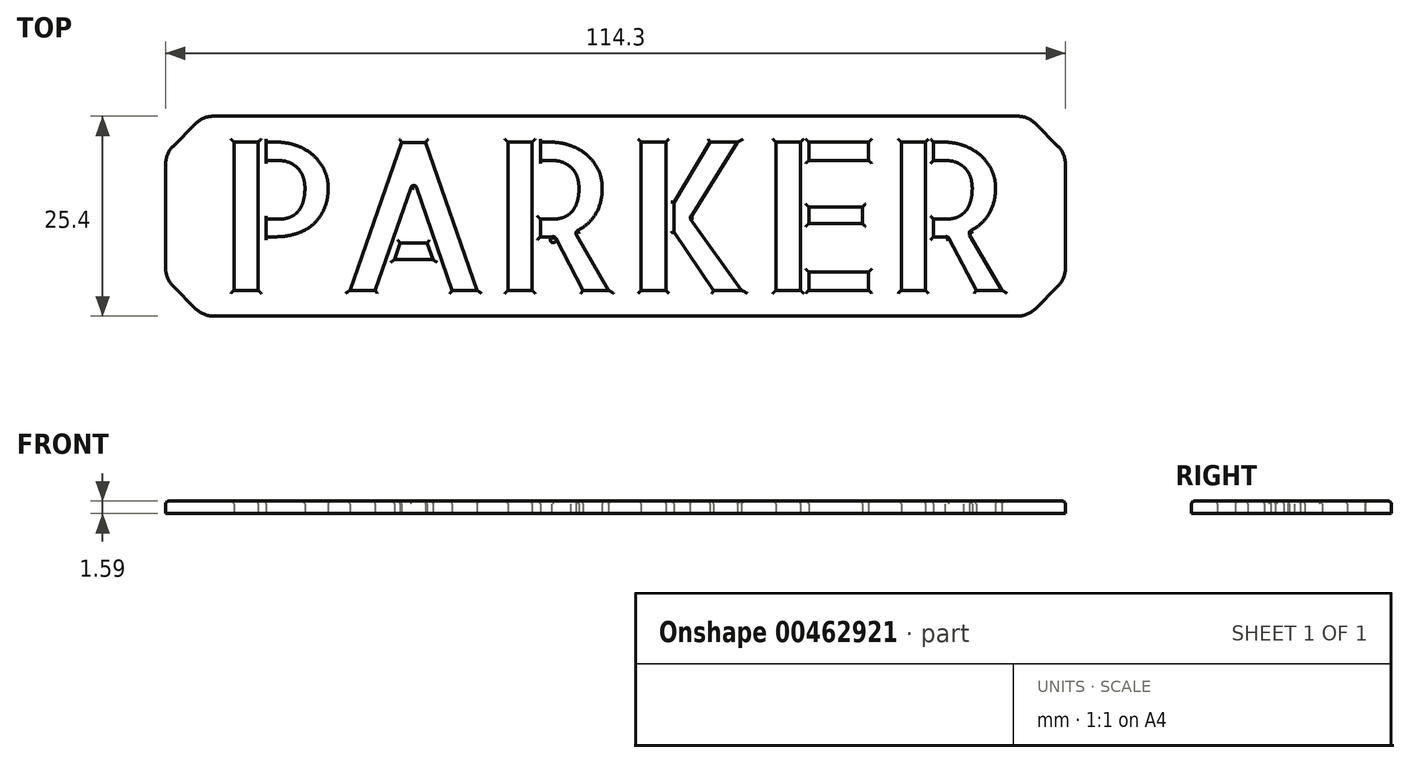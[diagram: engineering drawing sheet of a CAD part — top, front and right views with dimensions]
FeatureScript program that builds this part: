
annotation { "Feature Type Name" : "Feature", "Feature Type Description" : "" }
export const myFeature = defineFeature(function(context is Context, id is Id, definition is map)
    precondition{}
    {
        {
            var Q0;
            Q0=qCreatedBy(makeId("Top.planeOp"),FACE);
            var sketch = newSketch(context, id + "F0", { "sketchPlane" : qUnion([Q0])});
            skText(sketch, "E0", { "text": "PARKER", "fontName": "AllertaStencil-Regular.ttf"});
            skLineSegment(sketch, "E1.bottom", {"start": v(-6.35, 22.11) * mm, "end": v(107.95, 22.11) * mm});
            skLineSegment(sketch, "E1.top", {"start": v(-6.35, -3.29) * mm, "end": v(107.95, -3.29) * mm});
            skLineSegment(sketch, "E1.left", {"start": v(-6.35, 22.11) * mm, "end": v(-6.35, -3.29) * mm});
            skLineSegment(sketch, "E1.right", {"start": v(107.95, 22.11) * mm, "end": v(107.95, -3.29) * mm});
            skLineSegment(sketch, "E2", {"start": v(50.8, 18.83) * mm, "end": v(50.8, 22.11) * mm, "construction": true});
            skLineSegment(sketch, "E3", {"start": v(50.8, -3.29) * mm, "end": v(50.8, 0) * mm, "construction": true});
            const initialGuessF0  = {"E0": [0, 0, 1, 0, 0.01883]};
            skSetInitialGuess(sketch, initialGuessF0);
            skSolve(sketch);
        }
        {
            var Q0;
            Q0=qSketchRegion(id+"F0",true);
            extrude(context, id + "F1", {"entities" : qUnion([Q0]), "depth" : 1.59 * mm});
        }
        {
            var Q0;
            Q0=makeQuery(id+"F1.opExtrude","SWEPT_EDGE",EDGE,{"disambiguationData":[OSD([sQuery(id+"F0.wireOp",EDGE,"E1.bottom"),sQuery(id+"F0.wireOp",EDGE,"E1.right")])]});
            var Q1;
            Q1=makeQuery(id+"F1.opExtrude","SWEPT_EDGE",EDGE,{"disambiguationData":[OSD([sQuery(id+"F0.wireOp",EDGE,"E1.top"),sQuery(id+"F0.wireOp",EDGE,"E1.right")])]});
            var Q2;
            Q2=makeQuery(id+"F1.opExtrude","SWEPT_EDGE",EDGE,{"disambiguationData":[OSD([sQuery(id+"F0.wireOp",EDGE,"E1.top"),sQuery(id+"F0.wireOp",EDGE,"E1.left")])]});
            var Q3;
            Q3=makeQuery(id+"F1.opExtrude","SWEPT_EDGE",EDGE,{"disambiguationData":[OSD([sQuery(id+"F0.wireOp",EDGE,"E1.bottom"),sQuery(id+"F0.wireOp",EDGE,"E1.left")])]});
            chamfer(context, id + "F2", {"entities" : qUnion([Q0, Q1, Q2, Q3]), "width" : 4.76 * mm, "tangentPropagation" : true});
        }
        {
            var Q0;
            Q0=makeQuery(id+"F1.opExtrude","CAP_EDGE",EDGE,{"disambiguationData":[OSD([sQuery(id+"F0.wireOp",EDGE,"E0.sketch_text.stroke-17")])],"isStart":false});
            var Q1;
            Q1=makeQuery(id+"F1.opExtrude","CAP_EDGE",EDGE,{"disambiguationData":[OSD([sQuery(id+"F0.wireOp",EDGE,"E0.sketch_text.stroke-11")])],"isStart":false});
            var Q2;
            Q2=makeQuery(id+"F1.opExtrude","CAP_EDGE",EDGE,{"disambiguationData":[OSD([sQuery(id+"F0.wireOp",EDGE,"E0.sketch_text.stroke-10")])],"isStart":false});
            var Q3;
            Q3=makeQuery(id+"F1.opExtrude","CAP_EDGE",EDGE,{"disambiguationData":[OSD([sQuery(id+"F0.wireOp",EDGE,"E0.sketch_text.stroke-37")])],"isStart":false});
            var Q4;
            Q4=makeQuery(id+"F1.opExtrude","CAP_EDGE",EDGE,{"disambiguationData":[OSD([sQuery(id+"F0.wireOp",EDGE,"E0.sketch_text.stroke-29")])],"isStart":false});
            var Q5;
            Q5=makeQuery(id+"F1.opExtrude","CAP_EDGE",EDGE,{"disambiguationData":[OSD([sQuery(id+"F0.wireOp",EDGE,"E0.sketch_text.stroke-28")])],"isStart":false});
            var Q6;
            Q6=makeQuery(id+"F1.opExtrude","CAP_EDGE",EDGE,{"disambiguationData":[OSD([sQuery(id+"F0.wireOp",EDGE,"E0.sketch_text.stroke-18")])],"isStart":false});
            var Q7;
            Q7=makeQuery(id+"F1.opExtrude","CAP_EDGE",EDGE,{"disambiguationData":[OSD([sQuery(id+"F0.wireOp",EDGE,"E0.sketch_text.stroke-0")])],"isStart":false});
            var Q8;
            Q8=makeQuery(id+"F1.opExtrude","CAP_EDGE",EDGE,{"disambiguationData":[OSD([sQuery(id+"F0.wireOp",EDGE,"E0.sketch_text.stroke-3")])],"isStart":false});
            var Q9;
            Q9=makeQuery(id+"F1.opExtrude","CAP_EDGE",EDGE,{"disambiguationData":[OSD([sQuery(id+"F0.wireOp",EDGE,"E0.sketch_text.stroke-1")])],"isStart":false});
            var Q10;
            Q10=makeQuery(id+"F1.opExtrude","CAP_EDGE",EDGE,{"disambiguationData":[OSD([sQuery(id+"F0.wireOp",EDGE,"E0.sketch_text.stroke-2")])],"isStart":false});
            fillet(context, id + "F3", {"entities" : qUnion([Q0, Q1, Q2, Q3, Q4, Q5, Q6, Q7, Q8, Q9, Q10]), "radius" : 0.38 * mm, "tangentPropagation" : true, "allowEdgeOverflow" : false});
        }
        {
            var Q0;
            Q0=makeQuery(id+"F1.opExtrude","CAP_EDGE",EDGE,{"disambiguationData":[OSD([sQuery(id+"F0.wireOp",EDGE,"E0.sketch_text.stroke-53")])],"isStart":false});
            var Q1;
            Q1=makeQuery(id+"F1.opExtrude","CAP_EDGE",EDGE,{"disambiguationData":[OSD([sQuery(id+"F0.wireOp",EDGE,"E0.sketch_text.stroke-54")])],"isStart":false});
            var Q2;
            Q2=makeQuery(id+"F1.opExtrude","CAP_EDGE",EDGE,{"disambiguationData":[OSD([sQuery(id+"F0.wireOp",EDGE,"E0.sketch_text.stroke-64")])],"isStart":false});
            var Q3;
            Q3=makeQuery(id+"F1.opExtrude","CAP_EDGE",EDGE,{"disambiguationData":[OSD([sQuery(id+"F0.wireOp",EDGE,"E0.sketch_text.stroke-65")])],"isStart":false});
            var Q4;
            Q4=makeQuery(id+"F1.opExtrude","CAP_EDGE",EDGE,{"disambiguationData":[OSD([sQuery(id+"F0.wireOp",EDGE,"E0.sketch_text.stroke-72")])],"isStart":false});
            var Q5;
            Q5=makeQuery(id+"F1.opExtrude","CAP_EDGE",EDGE,{"disambiguationData":[OSD([sQuery(id+"F0.wireOp",EDGE,"E0.sketch_text.stroke-47")])],"isStart":false});
            var Q6;
            Q6=makeQuery(id+"F1.opExtrude","CAP_EDGE",EDGE,{"disambiguationData":[OSD([sQuery(id+"F0.wireOp",EDGE,"E0.sketch_text.stroke-48")])],"isStart":false});
            var Q7;
            Q7=makeQuery(id+"F1.opExtrude","CAP_EDGE",EDGE,{"disambiguationData":[OSD([sQuery(id+"F0.wireOp",EDGE,"E0.sketch_text.stroke-31")])],"isStart":false});
            var Q8;
            Q8=makeQuery(id+"F1.opExtrude","CAP_EDGE",EDGE,{"disambiguationData":[OSD([sQuery(id+"F0.wireOp",EDGE,"E0.sketch_text.stroke-30")])],"isStart":false});
            var Q9;
            Q9=makeQuery(id+"F1.opExtrude","CAP_EDGE",EDGE,{"disambiguationData":[OSD([sQuery(id+"F0.wireOp",EDGE,"E0.sketch_text.stroke-32")])],"isStart":false});
            var Q10;
            Q10=makeQuery(id+"F1.opExtrude","CAP_EDGE",EDGE,{"disambiguationData":[OSD([sQuery(id+"F0.wireOp",EDGE,"E0.sketch_text.stroke-26")])],"isStart":false});
            var Q11;
            Q11=makeQuery(id+"F1.opExtrude","CAP_EDGE",EDGE,{"disambiguationData":[OSD([sQuery(id+"F0.wireOp",EDGE,"E0.sketch_text.stroke-27")])],"isStart":false});
            var Q12;
            Q12=makeQuery(id+"F1.opExtrude","CAP_EDGE",EDGE,{"disambiguationData":[OSD([sQuery(id+"F0.wireOp",EDGE,"E0.sketch_text.stroke-36")])],"isStart":false});
            var Q13;
            Q13=makeQuery(id+"F1.opExtrude","CAP_EDGE",EDGE,{"disambiguationData":[OSD([sQuery(id+"F0.wireOp",EDGE,"E0.sketch_text.stroke-35")])],"isStart":false});
            var Q14;
            Q14=makeQuery(id+"F1.opExtrude","CAP_EDGE",EDGE,{"disambiguationData":[OSD([sQuery(id+"F0.wireOp",EDGE,"E0.sketch_text.stroke-34")])],"isStart":false});
            var Q15;
            Q15=makeQuery(id+"F1.opExtrude","CAP_EDGE",EDGE,{"disambiguationData":[OSD([sQuery(id+"F0.wireOp",EDGE,"E0.sketch_text.stroke-33")])],"isStart":false});
            fillet(context, id + "F4", {"entities" : qUnion([Q0, Q1, Q2, Q3, Q4, Q5, Q6, Q7, Q8, Q9, Q10, Q11, Q12, Q13, Q14, Q15]), "radius" : 0.38 * mm, "tangentPropagation" : true, "allowEdgeOverflow" : false});
        }
        {
            var Q0;
            Q0=makeQuery(id+"F1.opExtrude","CAP_EDGE",EDGE,{"disambiguationData":[OSD([sQuery(id+"F0.wireOp",EDGE,"E0.sketch_text.stroke-112")])],"isStart":false});
            var Q1;
            Q1=makeQuery(id+"F1.opExtrude","CAP_EDGE",EDGE,{"disambiguationData":[OSD([sQuery(id+"F0.wireOp",EDGE,"E0.sketch_text.stroke-122")])],"isStart":false});
            var Q2;
            Q2=makeQuery(id+"F1.opExtrude","CAP_EDGE",EDGE,{"disambiguationData":[OSD([sQuery(id+"F0.wireOp",EDGE,"E0.sketch_text.stroke-121")])],"isStart":false});
            var Q3;
            Q3=makeQuery(id+"F1.opExtrude","CAP_EDGE",EDGE,{"disambiguationData":[OSD([sQuery(id+"F0.wireOp",EDGE,"E0.sketch_text.stroke-117")])],"isStart":false});
            var Q4;
            Q4=makeQuery(id+"F1.opExtrude","CAP_EDGE",EDGE,{"disambiguationData":[OSD([sQuery(id+"F0.wireOp",EDGE,"E0.sketch_text.stroke-113")])],"isStart":false});
            var Q5;
            Q5=makeQuery(id+"F1.opExtrude","CAP_EDGE",EDGE,{"disambiguationData":[OSD([sQuery(id+"F0.wireOp",EDGE,"E0.sketch_text.stroke-144")])],"isStart":false});
            var Q6;
            Q6=makeQuery(id+"F1.opExtrude","CAP_EDGE",EDGE,{"disambiguationData":[OSD([sQuery(id+"F0.wireOp",EDGE,"E0.sketch_text.stroke-143")])],"isStart":false});
            var Q7;
            Q7=makeQuery(id+"F1.opExtrude","CAP_EDGE",EDGE,{"disambiguationData":[OSD([sQuery(id+"F0.wireOp",EDGE,"E0.sketch_text.stroke-139")])],"isStart":false});
            var Q8;
            Q8=makeQuery(id+"F1.opExtrude","CAP_EDGE",EDGE,{"disambiguationData":[OSD([sQuery(id+"F0.wireOp",EDGE,"E0.sketch_text.stroke-135")])],"isStart":false});
            var Q9;
            Q9=makeQuery(id+"F1.opExtrude","CAP_EDGE",EDGE,{"disambiguationData":[OSD([sQuery(id+"F0.wireOp",EDGE,"E0.sketch_text.stroke-134")])],"isStart":false});
            fillet(context, id + "F5", {"entities" : qUnion([Q0, Q1, Q2, Q3, Q4, Q5, Q6, Q7, Q8, Q9]), "radius" : 0.38 * mm, "tangentPropagation" : true, "allowEdgeOverflow" : false});
        }
        {
            var Q0;
            {var subQ0=sQuery(id+"F0.wireOp",EDGE,"E1.bottom");Q0=makeQuery(id+"F2.opChamfer","BLEND_EDGE",EDGE,{"blendedFrom":[makeQuery(id+"F1.opExtrude","SWEPT_EDGE",EDGE,{"disambiguationData":[OSD([subQ0,sQuery(id+"F0.wireOp",EDGE,"E1.right")])]}),makeQuery(id+"F1.opExtrude","SWEPT_FACE",FACE,{"disambiguationData":[OSD([subQ0])]})],"blendedInto":[makeQuery(id+"F1.opExtrude","SWEPT_FACE",FACE,{"disambiguationData":[OSD([subQ0])]})]});}
            var Q1;
            {var subQ0=sQuery(id+"F0.wireOp",EDGE,"E1.right");Q1=makeQuery(id+"F2.opChamfer","BLEND_EDGE",EDGE,{"blendedFrom":[makeQuery(id+"F1.opExtrude","SWEPT_EDGE",EDGE,{"disambiguationData":[OSD([sQuery(id+"F0.wireOp",EDGE,"E1.bottom"),subQ0])]}),makeQuery(id+"F1.opExtrude","SWEPT_FACE",FACE,{"disambiguationData":[OSD([subQ0])]})],"blendedInto":[makeQuery(id+"F1.opExtrude","SWEPT_FACE",FACE,{"disambiguationData":[OSD([subQ0])]})]});}
            var Q2;
            {var subQ0=sQuery(id+"F0.wireOp",EDGE,"E1.right");Q2=makeQuery(id+"F2.opChamfer","BLEND_EDGE",EDGE,{"blendedFrom":[makeQuery(id+"F1.opExtrude","SWEPT_EDGE",EDGE,{"disambiguationData":[OSD([sQuery(id+"F0.wireOp",EDGE,"E1.top"),subQ0])]}),makeQuery(id+"F1.opExtrude","SWEPT_FACE",FACE,{"disambiguationData":[OSD([subQ0])]})],"blendedInto":[makeQuery(id+"F1.opExtrude","SWEPT_FACE",FACE,{"disambiguationData":[OSD([subQ0])]})]});}
            var Q3;
            {var subQ0=sQuery(id+"F0.wireOp",EDGE,"E1.top");Q3=makeQuery(id+"F2.opChamfer","BLEND_EDGE",EDGE,{"blendedFrom":[makeQuery(id+"F1.opExtrude","SWEPT_EDGE",EDGE,{"disambiguationData":[OSD([subQ0,sQuery(id+"F0.wireOp",EDGE,"E1.right")])]}),makeQuery(id+"F1.opExtrude","SWEPT_FACE",FACE,{"disambiguationData":[OSD([subQ0])]})],"blendedInto":[makeQuery(id+"F1.opExtrude","SWEPT_FACE",FACE,{"disambiguationData":[OSD([subQ0])]})]});}
            var Q4;
            {var subQ0=sQuery(id+"F0.wireOp",EDGE,"E1.top");Q4=makeQuery(id+"F2.opChamfer","BLEND_EDGE",EDGE,{"blendedFrom":[makeQuery(id+"F1.opExtrude","SWEPT_EDGE",EDGE,{"disambiguationData":[OSD([subQ0,sQuery(id+"F0.wireOp",EDGE,"E1.left")])]}),makeQuery(id+"F1.opExtrude","SWEPT_FACE",FACE,{"disambiguationData":[OSD([subQ0])]})],"blendedInto":[makeQuery(id+"F1.opExtrude","SWEPT_FACE",FACE,{"disambiguationData":[OSD([subQ0])]})]});}
            var Q5;
            {var subQ0=sQuery(id+"F0.wireOp",EDGE,"E1.left");Q5=makeQuery(id+"F2.opChamfer","BLEND_EDGE",EDGE,{"blendedFrom":[makeQuery(id+"F1.opExtrude","SWEPT_EDGE",EDGE,{"disambiguationData":[OSD([sQuery(id+"F0.wireOp",EDGE,"E1.top"),subQ0])]}),makeQuery(id+"F1.opExtrude","SWEPT_FACE",FACE,{"disambiguationData":[OSD([subQ0])]})],"blendedInto":[makeQuery(id+"F1.opExtrude","SWEPT_FACE",FACE,{"disambiguationData":[OSD([subQ0])]})]});}
            var Q6;
            {var subQ0=sQuery(id+"F0.wireOp",EDGE,"E1.left");Q6=makeQuery(id+"F2.opChamfer","BLEND_EDGE",EDGE,{"blendedFrom":[makeQuery(id+"F1.opExtrude","SWEPT_EDGE",EDGE,{"disambiguationData":[OSD([sQuery(id+"F0.wireOp",EDGE,"E1.bottom"),subQ0])]}),makeQuery(id+"F1.opExtrude","SWEPT_FACE",FACE,{"disambiguationData":[OSD([subQ0])]})],"blendedInto":[makeQuery(id+"F1.opExtrude","SWEPT_FACE",FACE,{"disambiguationData":[OSD([subQ0])]})]});}
            var Q7;
            {var subQ0=sQuery(id+"F0.wireOp",EDGE,"E1.bottom");Q7=makeQuery(id+"F2.opChamfer","BLEND_EDGE",EDGE,{"blendedFrom":[makeQuery(id+"F1.opExtrude","SWEPT_EDGE",EDGE,{"disambiguationData":[OSD([subQ0,sQuery(id+"F0.wireOp",EDGE,"E1.left")])]}),makeQuery(id+"F1.opExtrude","SWEPT_FACE",FACE,{"disambiguationData":[OSD([subQ0])]})],"blendedInto":[makeQuery(id+"F1.opExtrude","SWEPT_FACE",FACE,{"disambiguationData":[OSD([subQ0])]})]});}
            fillet(context, id + "F6", {"entities" : qUnion([Q0, Q1, Q2, Q3, Q4, Q5, Q6, Q7]), "radius" : 3.17 * mm, "tangentPropagation" : true, "allowEdgeOverflow" : false});
        }
        {
            var Q0;
            Q0=makeQuery(id+"F1.opExtrude","CAP_EDGE",EDGE,{"disambiguationData":[OSD([sQuery(id+"F0.wireOp",EDGE,"E1.bottom")])],"isStart":false});
            fillet(context, id + "F7", {"entities" : qUnion([Q0]), "radius" : 0.38 * mm, "tangentPropagation" : true, "allowEdgeOverflow" : false});
        }
        {
            var Q0;
            Q0=makeQuery(id+"F1.opExtrude","CAP_EDGE",EDGE,{"disambiguationData":[OSD([sQuery(id+"F0.wireOp",EDGE,"E0.sketch_text.stroke-40")])],"isStart":false});
            var Q1;
            Q1=makeQuery(id+"F1.opExtrude","CAP_EDGE",EDGE,{"disambiguationData":[OSD([sQuery(id+"F0.wireOp",EDGE,"E0.sketch_text.stroke-38")])],"isStart":false});
            var Q2;
            Q2=makeQuery(id+"F1.opExtrude","CAP_EDGE",EDGE,{"disambiguationData":[OSD([sQuery(id+"F0.wireOp",EDGE,"E0.sketch_text.stroke-39")])],"isStart":false});
            var Q3;
            Q3=makeQuery(id+"F1.opExtrude","CAP_EDGE",EDGE,{"disambiguationData":[OSD([sQuery(id+"F0.wireOp",EDGE,"E0.sketch_text.stroke-67")])],"isStart":false});
            var Q4;
            Q4=makeQuery(id+"F1.opExtrude","CAP_EDGE",EDGE,{"disambiguationData":[OSD([sQuery(id+"F0.wireOp",EDGE,"E0.sketch_text.stroke-68")])],"isStart":false});
            var Q5;
            Q5=makeQuery(id+"F1.opExtrude","CAP_EDGE",EDGE,{"disambiguationData":[OSD([sQuery(id+"F0.wireOp",EDGE,"E0.sketch_text.stroke-69")])],"isStart":false});
            var Q6;
            Q6=makeQuery(id+"F1.opExtrude","CAP_EDGE",EDGE,{"disambiguationData":[OSD([sQuery(id+"F0.wireOp",EDGE,"E0.sketch_text.stroke-70")])],"isStart":false});
            var Q7;
            Q7=makeQuery(id+"F1.opExtrude","CAP_EDGE",EDGE,{"disambiguationData":[OSD([sQuery(id+"F0.wireOp",EDGE,"E0.sketch_text.stroke-75")])],"isStart":false});
            var Q8;
            Q8=makeQuery(id+"F1.opExtrude","CAP_EDGE",EDGE,{"disambiguationData":[OSD([sQuery(id+"F0.wireOp",EDGE,"E0.sketch_text.stroke-76")])],"isStart":false});
            var Q9;
            Q9=makeQuery(id+"F1.opExtrude","CAP_EDGE",EDGE,{"disambiguationData":[OSD([sQuery(id+"F0.wireOp",EDGE,"E0.sketch_text.stroke-77")])],"isStart":false});
            var Q10;
            Q10=makeQuery(id+"F1.opExtrude","CAP_EDGE",EDGE,{"disambiguationData":[OSD([sQuery(id+"F0.wireOp",EDGE,"E0.sketch_text.stroke-71")])],"isStart":false});
            var Q11;
            Q11=makeQuery(id+"F1.opExtrude","CAP_EDGE",EDGE,{"disambiguationData":[OSD([sQuery(id+"F0.wireOp",EDGE,"E0.sketch_text.stroke-73")])],"isStart":false});
            var Q12;
            Q12=makeQuery(id+"F1.opExtrude","CAP_EDGE",EDGE,{"disambiguationData":[OSD([sQuery(id+"F0.wireOp",EDGE,"E0.sketch_text.stroke-74")])],"isStart":false});
            var Q13;
            Q13=makeQuery(id+"F1.opExtrude","CAP_EDGE",EDGE,{"disambiguationData":[OSD([sQuery(id+"F0.wireOp",EDGE,"E0.sketch_text.stroke-81")])],"isStart":false});
            var Q14;
            Q14=makeQuery(id+"F1.opExtrude","CAP_EDGE",EDGE,{"disambiguationData":[OSD([sQuery(id+"F0.wireOp",EDGE,"E0.sketch_text.stroke-78")])],"isStart":false});
            var Q15;
            Q15=makeQuery(id+"F1.opExtrude","CAP_EDGE",EDGE,{"disambiguationData":[OSD([sQuery(id+"F0.wireOp",EDGE,"E0.sketch_text.stroke-79")])],"isStart":false});
            var Q16;
            Q16=makeQuery(id+"F1.opExtrude","CAP_EDGE",EDGE,{"disambiguationData":[OSD([sQuery(id+"F0.wireOp",EDGE,"E0.sketch_text.stroke-80")])],"isStart":false});
            var Q17;
            Q17=makeQuery(id+"F1.opExtrude","CAP_EDGE",EDGE,{"disambiguationData":[OSD([sQuery(id+"F0.wireOp",EDGE,"E0.sketch_text.stroke-91")])],"isStart":false});
            var Q18;
            Q18=makeQuery(id+"F1.opExtrude","CAP_EDGE",EDGE,{"disambiguationData":[OSD([sQuery(id+"F0.wireOp",EDGE,"E0.sketch_text.stroke-90")])],"isStart":false});
            var Q19;
            Q19=makeQuery(id+"F1.opExtrude","CAP_EDGE",EDGE,{"disambiguationData":[OSD([sQuery(id+"F0.wireOp",EDGE,"E0.sketch_text.stroke-93")])],"isStart":false});
            var Q20;
            Q20=makeQuery(id+"F1.opExtrude","CAP_EDGE",EDGE,{"disambiguationData":[OSD([sQuery(id+"F0.wireOp",EDGE,"E0.sketch_text.stroke-92")])],"isStart":false});
            var Q21;
            Q21=makeQuery(id+"F1.opExtrude","CAP_EDGE",EDGE,{"disambiguationData":[OSD([sQuery(id+"F0.wireOp",EDGE,"E0.sketch_text.stroke-83")])],"isStart":false});
            var Q22;
            Q22=makeQuery(id+"F1.opExtrude","CAP_EDGE",EDGE,{"disambiguationData":[OSD([sQuery(id+"F0.wireOp",EDGE,"E0.sketch_text.stroke-84")])],"isStart":false});
            var Q23;
            Q23=makeQuery(id+"F1.opExtrude","CAP_EDGE",EDGE,{"disambiguationData":[OSD([sQuery(id+"F0.wireOp",EDGE,"E0.sketch_text.stroke-82")])],"isStart":false});
            var Q24;
            Q24=makeQuery(id+"F1.opExtrude","CAP_EDGE",EDGE,{"disambiguationData":[OSD([sQuery(id+"F0.wireOp",EDGE,"E0.sketch_text.stroke-85")])],"isStart":false});
            var Q25;
            Q25=makeQuery(id+"F1.opExtrude","CAP_EDGE",EDGE,{"disambiguationData":[OSD([sQuery(id+"F0.wireOp",EDGE,"E0.sketch_text.stroke-87")])],"isStart":false});
            var Q26;
            Q26=makeQuery(id+"F1.opExtrude","CAP_EDGE",EDGE,{"disambiguationData":[OSD([sQuery(id+"F0.wireOp",EDGE,"E0.sketch_text.stroke-86")])],"isStart":false});
            var Q27;
            Q27=makeQuery(id+"F1.opExtrude","CAP_EDGE",EDGE,{"disambiguationData":[OSD([sQuery(id+"F0.wireOp",EDGE,"E0.sketch_text.stroke-88")])],"isStart":false});
            var Q28;
            Q28=makeQuery(id+"F1.opExtrude","CAP_EDGE",EDGE,{"disambiguationData":[OSD([sQuery(id+"F0.wireOp",EDGE,"E0.sketch_text.stroke-89")])],"isStart":false});
            fillet(context, id + "F8", {"entities" : qUnion([Q0, Q1, Q2, Q3, Q4, Q5, Q6, Q7, Q8, Q9, Q10, Q11, Q12, Q13, Q14, Q15, Q16, Q17, Q18, Q19, Q20, Q21, Q22, Q23, Q24, Q25, Q26, Q27, Q28]), "radius" : 0.38 * mm, "tangentPropagation" : true, "allowEdgeOverflow" : false});
        }
        {
            var Q0;
            Q0=makeQuery(id+"F1.opExtrude","CAP_EDGE",EDGE,{"disambiguationData":[OSD([sQuery(id+"F0.wireOp",EDGE,"E0.sketch_text.stroke-97")])],"isStart":false});
            var Q1;
            Q1=makeQuery(id+"F1.opExtrude","CAP_EDGE",EDGE,{"disambiguationData":[OSD([sQuery(id+"F0.wireOp",EDGE,"E0.sketch_text.stroke-94")])],"isStart":false});
            var Q2;
            Q2=makeQuery(id+"F1.opExtrude","CAP_EDGE",EDGE,{"disambiguationData":[OSD([sQuery(id+"F0.wireOp",EDGE,"E0.sketch_text.stroke-95")])],"isStart":false});
            var Q3;
            Q3=makeQuery(id+"F1.opExtrude","CAP_EDGE",EDGE,{"disambiguationData":[OSD([sQuery(id+"F0.wireOp",EDGE,"E0.sketch_text.stroke-96")])],"isStart":false});
            var Q4;
            Q4=makeQuery(id+"F1.opExtrude","CAP_EDGE",EDGE,{"disambiguationData":[OSD([sQuery(id+"F0.wireOp",EDGE,"E0.sketch_text.stroke-115")])],"isStart":false});
            var Q5;
            Q5=makeQuery(id+"F1.opExtrude","CAP_EDGE",EDGE,{"disambiguationData":[OSD([sQuery(id+"F0.wireOp",EDGE,"E0.sketch_text.stroke-104")])],"isStart":false});
            var Q6;
            Q6=makeQuery(id+"F1.opExtrude","CAP_EDGE",EDGE,{"disambiguationData":[OSD([sQuery(id+"F0.wireOp",EDGE,"E0.sketch_text.stroke-99")])],"isStart":false});
            var Q7;
            Q7=makeQuery(id+"F1.opExtrude","CAP_EDGE",EDGE,{"disambiguationData":[OSD([sQuery(id+"F0.wireOp",EDGE,"E0.sketch_text.stroke-98")])],"isStart":false});
            var Q8;
            Q8=makeQuery(id+"F1.opExtrude","CAP_EDGE",EDGE,{"disambiguationData":[OSD([sQuery(id+"F0.wireOp",EDGE,"E0.sketch_text.stroke-123")])],"isStart":false});
            fillet(context, id + "F9", {"entities" : qUnion([Q0, Q1, Q2, Q3, Q4, Q5, Q6, Q7, Q8]), "radius" : 0.38 * mm, "tangentPropagation" : true, "allowEdgeOverflow" : false});
        }
        {
            var Q0;
            Q0=makeQuery(id+"F1.opExtrude","CAP_EDGE",EDGE,{"disambiguationData":[OSD([sQuery(id+"F0.wireOp",EDGE,"E0.sketch_text.stroke-46")])],"isStart":false});
            fillet(context, id + "F10", {"entities" : qUnion([Q0]), "radius" : 0.38 * mm, "tangentPropagation" : true, "allowEdgeOverflow" : false});
        }
        {
            var Q0;
            Q0=makeQuery(id+"F1.opExtrude","CAP_EDGE",EDGE,{"disambiguationData":[OSD([sQuery(id+"F0.wireOp",EDGE,"E0.sketch_text.stroke-42")])],"isStart":false});
            var Q1;
            Q1=makeQuery(id+"F1.opExtrude","CAP_EDGE",EDGE,{"disambiguationData":[OSD([sQuery(id+"F0.wireOp",EDGE,"E0.sketch_text.stroke-41")])],"isStart":false});
            var Q2;
            Q2=makeQuery(id+"F1.opExtrude","CAP_EDGE",EDGE,{"disambiguationData":[OSD([sQuery(id+"F0.wireOp",EDGE,"E0.sketch_text.stroke-66")])],"isStart":false});
            fillet(context, id + "F11", {"entities" : qUnion([Q0, Q1, Q2]), "radius" : 0.38 * mm, "tangentPropagation" : true, "allowEdgeOverflow" : false});
        }
        {
            var Q0;
            Q0=makeQuery(id+"F1.opExtrude","CAP_EDGE",EDGE,{"disambiguationData":[OSD([sQuery(id+"F0.wireOp",EDGE,"E0.sketch_text.stroke-103")])],"isStart":false});
            fillet(context, id + "F12", {"entities" : qUnion([Q0]), "radius" : 0.38 * mm, "tangentPropagation" : true, "allowEdgeOverflow" : false});
        }
    });
